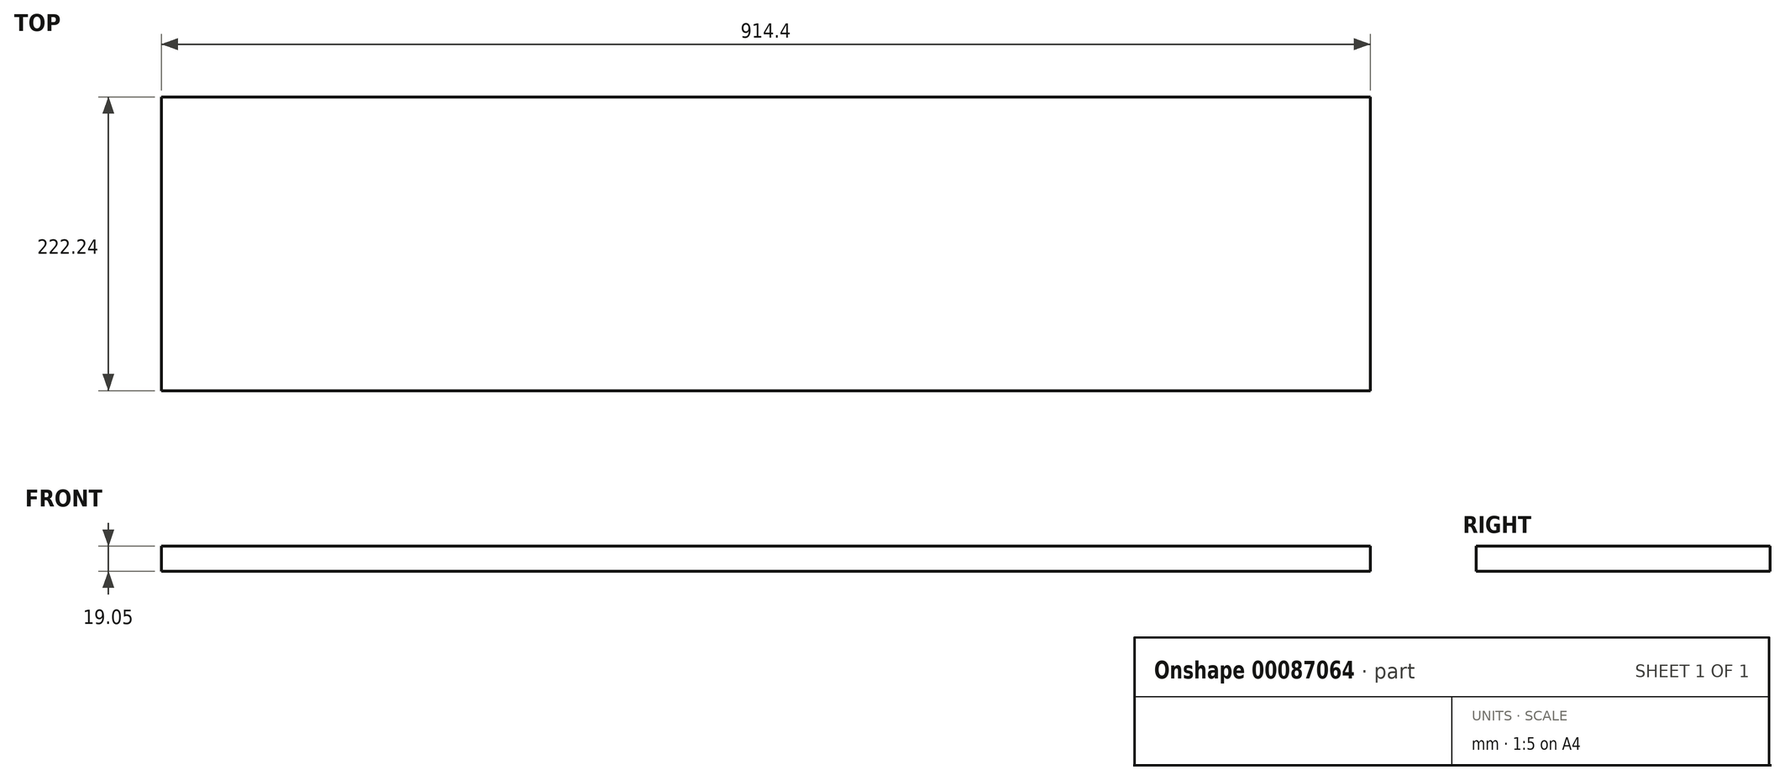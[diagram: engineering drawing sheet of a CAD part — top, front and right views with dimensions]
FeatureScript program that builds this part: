
annotation { "Feature Type Name" : "Feature", "Feature Type Description" : "" }
export const myFeature = defineFeature(function(context is Context, id is Id, definition is map)
    precondition{}
    {
        {
            var Q0;
            Q0=qCreatedBy(makeId("Top.planeOp"),FACE);
            var sketch = newSketch(context, id + "F0", { "sketchPlane" : qUnion([Q0])});
            skLineSegment(sketch, "E0.bottom", {"start": v(-457.2, 111.13) * mm, "end": v(457.2, 111.13) * mm});
            skLineSegment(sketch, "E0.top", {"start": v(-457.2, -111.13) * mm, "end": v(457.2, -111.13) * mm});
            skLineSegment(sketch, "E0.left", {"start": v(-457.2, 111.13) * mm, "end": v(-457.2, -111.13) * mm});
            skLineSegment(sketch, "E0.right", {"start": v(457.2, 111.13) * mm, "end": v(457.2, -111.13) * mm});
            skPoint(sketch, "E0.middle", {"position": v(0, 0) * mm});
            skSolve(sketch);
        }
        {
            var Q0;
            Q0=makeQuery(id+"F0.imprint","IMPRINT",FACE,{"disambiguationData":[TD([[makeQuery(id+"F0.imprint","IMPRINT",EDGE,{"derivedFrom":sQuery(id+"F0.wireOp",EDGE,"E0.bottom")}),-1.0]])]});
            extrude(context, id + "F1", {"entities" : qUnion([Q0]), "depth" : 19.05 * mm});
        }
    });
